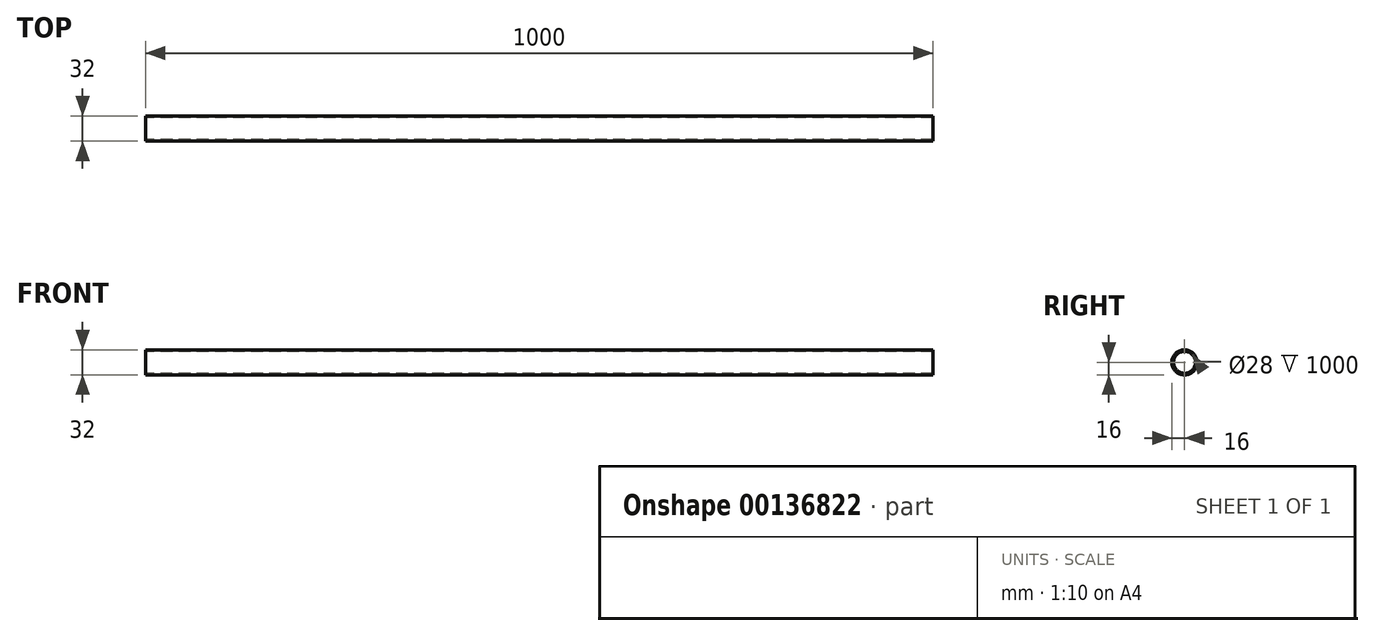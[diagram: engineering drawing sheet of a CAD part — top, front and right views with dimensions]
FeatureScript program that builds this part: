
annotation { "Feature Type Name" : "Feature", "Feature Type Description" : "" }
export const myFeature = defineFeature(function(context is Context, id is Id, definition is map)
    precondition{}
    {
        {
            var Q0;
            Q0=qCreatedBy(makeId("Right.planeOp"),FACE);
            var sketch = newSketch(context, id + "F0", { "sketchPlane" : qUnion([Q0])});
            skCircle(sketch, "E0", {"center": v(0, 0) * mm, "radius": 16 * mm});
            skCircle(sketch, "E1", {"center": v(0, 0) * mm, "radius": 14 * mm});
            skSolve(sketch);
        }
        {
            var Q0;
            Q0=makeQuery(id+"F0.imprint","IMPRINT",FACE,{"disambiguationData":[TD([[makeQuery(id+"F0.imprint","IMPRINT",EDGE,{"derivedFrom":sQuery(id+"F0.wireOp",EDGE,"E0")}),1.0]])]});
            extrude(context, id + "F1", {"entities" : qUnion([Q0]), "endBound" : BoundingType.SYMMETRIC, "depth" : 1000 * mm});
        }
    });
